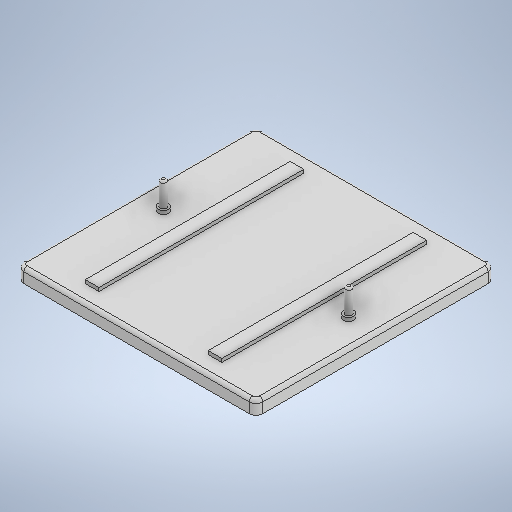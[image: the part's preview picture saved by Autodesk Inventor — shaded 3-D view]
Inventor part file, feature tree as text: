
AUTODESK INVENTOR PART (.ipt)
format: ipt  version: 2025 (Build 290162000, 162)  size: 275,456 bytes
history: native  units: mm
features: extrude x3, fillet x3, sketch x3
ambient origin geometry x8: Origin, YZ Plane, XZ Plane, XY Plane, X Axis, Y Axis, Z Axis, Center Point
bodies: Solid1 (feature_tree)
feature tree (9):
  extrude  "Extrusion1"  Depth=70.0mm
  extrude  "Extrusion2"  Depth=4.0mm
  fillet  "Fillet1"  Radius=1.8mm
  fillet  "Fillet2"  Radius=54.3mm
  extrude  "Extrusion3"  Depth=8.0mm TaperAngle=0.0deg
  fillet  "Fillet3"  Radius=2.0mm
  sketch  "Sketch1"  dims[d0=70.0mm d1=70.0mm]
  sketch  "Sketch2"  dims[d2=4.0mm d3=0.0mm d4=1.8mm d5=1.8mm d6=54.3mm]
  sketch  "Sketch3"  dims[d7=27.15mm d8=8.0mm d9=0.0mm d10=2.0mm d11=0.5mm d12=18.0mm d13=60.0mm d14=60.0mm d15=18.0mm d16=4.0mm d17=4.0mm d18=3.0mm d19=3.0mm d20=1.0mm d21=0.0mm d22=1.0mm]
